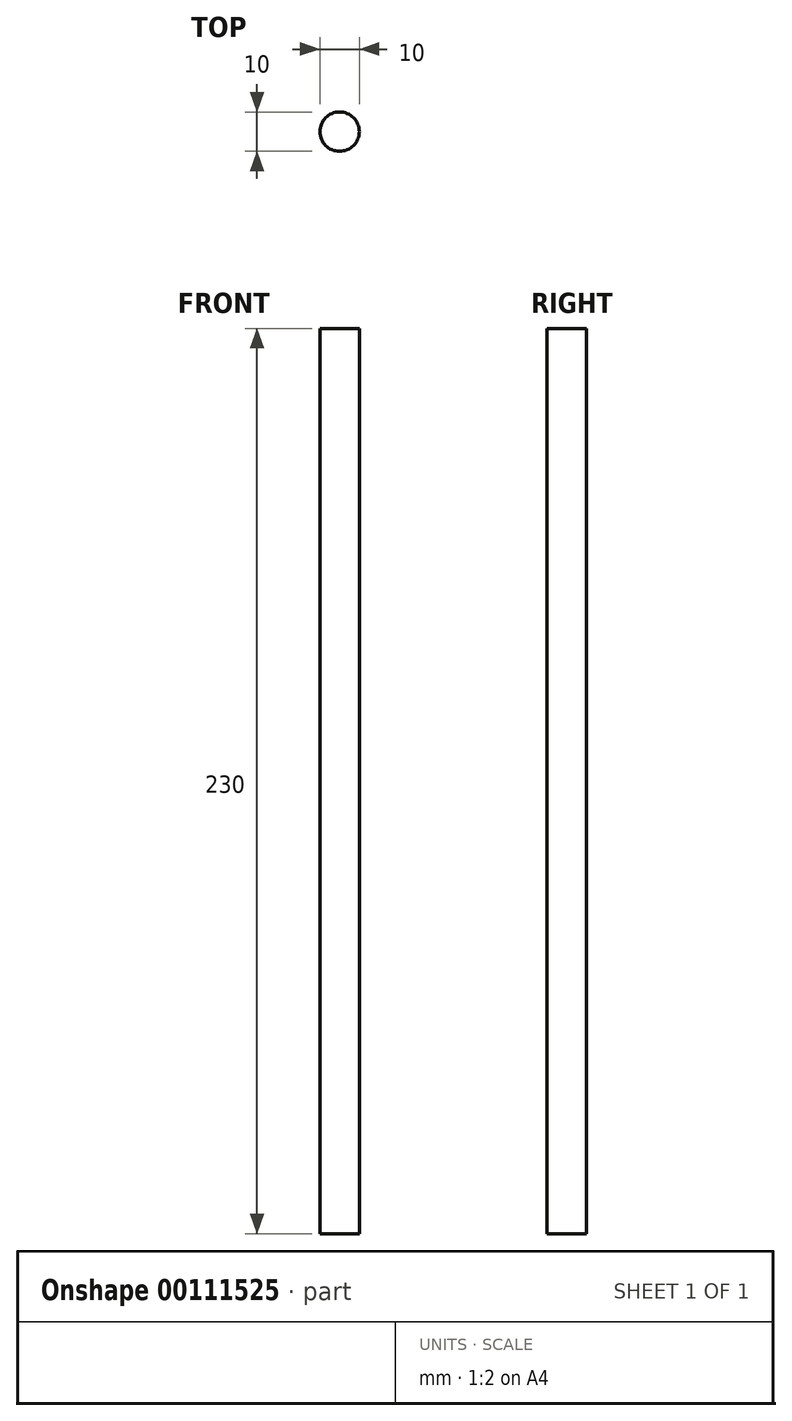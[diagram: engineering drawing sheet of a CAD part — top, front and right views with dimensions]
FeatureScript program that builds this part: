
annotation { "Feature Type Name" : "Feature", "Feature Type Description" : "" }
export const myFeature = defineFeature(function(context is Context, id is Id, definition is map)
    precondition{}
    {
        {
            var Q0;
            Q0=qCreatedBy(makeId("Top.planeOp"),FACE);
            var sketch = newSketch(context, id + "F0", { "sketchPlane" : qUnion([Q0])});
            skCircle(sketch, "E0", {"center": v(0, 0) * mm, "radius": 5 * mm});
            skSolve(sketch);
        }
        {
            var Q0;
            Q0=makeQuery(id+"F0.imprint","IMPRINT",FACE,{"disambiguationData":[TD([[makeQuery(id+"F0.imprint","IMPRINT",EDGE,{"derivedFrom":sQuery(id+"F0.wireOp",EDGE,"E0")}),1.0]])]});
            extrude(context, id + "F1", {"entities" : qUnion([Q0]), "depth" : 230 * mm});
        }
    });
